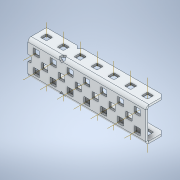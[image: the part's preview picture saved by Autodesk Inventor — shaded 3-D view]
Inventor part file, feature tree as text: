
AUTODESK INVENTOR PART (.ipt)
format: ipt  version: 2020 (Build 240168000, 168)  size: 1,208,832 bytes
history: native  units: in
note: dims shown in document units (in); Inventor stores cm internally (conversion verified against a paired STEP export)
features: other x38, plane x10, pattern_linear x4, split x4, sheet_metal_op x1
ambient origin geometry x8: Origin, YZ Plane, XZ Plane, XY Plane, X Axis, Y Axis, Z Axis, Center Point
bodies: Solid1 (feature_tree)
feature tree (57):
  other  "Work Axis1"
  pattern_linear  "Rectangular Pattern1"  Count1=7 Spacing1=0.5in
  other  "Work Axis72"
  pattern_linear  "Rectangular Pattern2"  Count1=7 Spacing1=0.5in
  pattern_linear  "Rectangular Pattern3"  Count1=7 Spacing1=0.5in
  other  "Work Axis141"
  pattern_linear  "Rectangular Pattern4"  Count1=6 Spacing1=0.5in
  plane  "Work Plane7"
  split  "Split1"
  plane  "Work Plane8"
  split  "Split2"
  plane  "Work Plane9"
  split  "Split3"
  plane  "Work Plane10"
  split  "Split4"
  plane  "Work Plane1"
  plane  "Work Plane2"
  other  "Work Point1"
  other  "Work Axis2"
  other  "Work Axis3"
  other  "Work Axis4"
  other  "Work Axis5"
  other  "Work Axis6"
  other  "Work Axis7"
  other  "Work Axis36"
  other  "Work Axis37"
  other  "Work Axis38"
  other  "Work Axis39"
  other  "Work Axis40"
  other  "Work Axis41"
  other  "Work Axis42"
  plane  "Work Plane3"
  plane  "Work Plane4"
  other  "Work Point2"
  other  "Work Axis71"
  other  "Work Point3"
  other  "Work Axis73"
  other  "Work Axis74"
  other  "Work Axis75"
  other  "Work Axis76"
  other  "Work Axis77"
  other  "Work Axis78"
  other  "Work Axis107"
  other  "Work Axis108"
  other  "Work Axis109"
  other  "Work Axis110"
  plane  "Work Plane5"
  plane  "Work Plane6"
  other  "Work Point4"
  other  "Work Axis142"
  other  "Work Axis143"
  other  "Work Axis144"
  other  "Work Axis145"
  other  "Work Axis146"
  other  "Work Axis175"
  other  "Work Axis176"
  sheet_metal_op  "Fold1"
